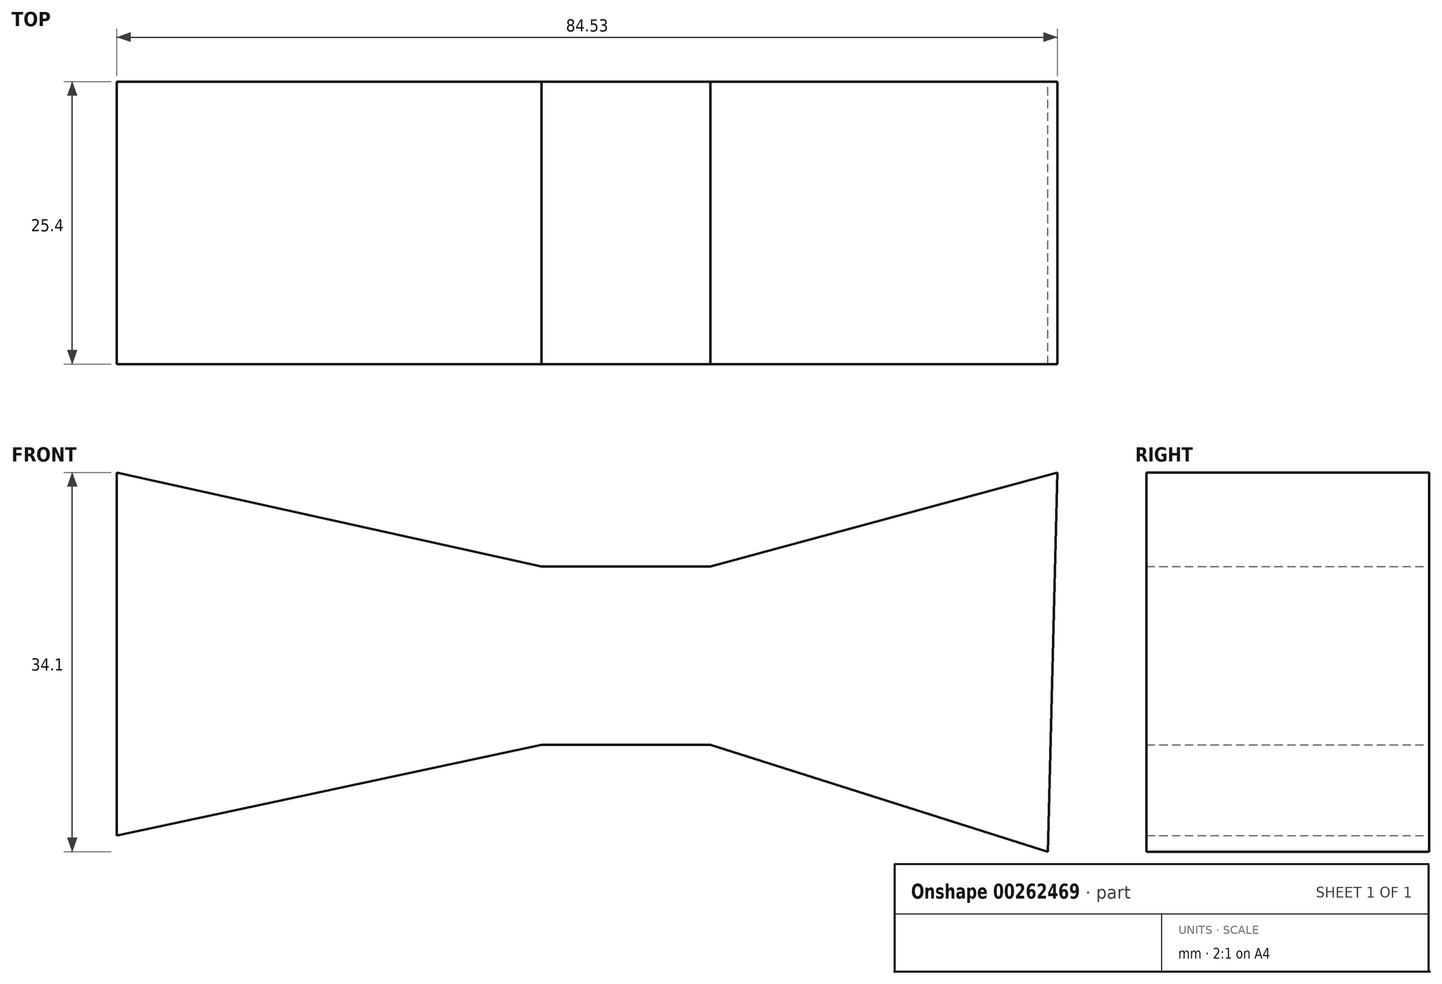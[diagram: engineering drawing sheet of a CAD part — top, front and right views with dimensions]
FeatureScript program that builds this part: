
annotation { "Feature Type Name" : "Feature", "Feature Type Description" : "" }
export const myFeature = defineFeature(function(context is Context, id is Id, definition is map)
    precondition{}
    {
        {
            var Q0;
            Q0=qCreatedBy(makeId("Front.planeOp"),FACE);
            var sketch = newSketch(context, id + "F0", { "sketchPlane" : qUnion([Q0])});
            skLineSegment(sketch, "E0.bottom", {"start": v(7.58, -8.02) * mm, "end": v(-7.58, -8.02) * mm});
            skLineSegment(sketch, "E0.top", {"start": v(7.58, 8.02) * mm, "end": v(-7.58, 8.02) * mm});
            skLineSegment(sketch, "E0.left", {"start": v(7.58, -8.02) * mm, "end": v(7.58, 8.02) * mm});
            skLineSegment(sketch, "E0.right", {"start": v(-7.58, -8.02) * mm, "end": v(-7.58, 8.02) * mm});
            skPoint(sketch, "E0.middle", {"position": v(0, 0) * mm});
            skLineSegment(sketch, "E1", {"start": v(-7.58, 8.02) * mm, "end": v(-45.76, 16.47) * mm});
            skLineSegment(sketch, "E2", {"start": v(-45.76, 16.47) * mm, "end": v(-45.76, -16.18) * mm});
            skLineSegment(sketch, "E3", {"start": v(-45.76, -16.18) * mm, "end": v(-7.58, -8.02) * mm});
            skLineSegment(sketch, "E4", {"start": v(7.58, 8.02) * mm, "end": v(38.77, 16.47) * mm});
            skLineSegment(sketch, "E5", {"start": v(7.58, -8.02) * mm, "end": v(37.9, -17.63) * mm});
            skLineSegment(sketch, "E6", {"start": v(37.9, -17.63) * mm, "end": v(38.77, 16.47) * mm});
            skSolve(sketch);
        }
        {
            var Q0;
            Q0 = qSketchRegion(id + "F0", true);
            extrude(context, id + "F1", {"entities" : qUnion([Q0]), "depth" : 25.4 * mm});
        }
        {
            var Q0;
            Q0 = qSketchRegion(id + "F0", true);
            extrude(context, id + "F2", {"entities" : qUnion([Q0]), "operationType" : NewBodyOperationType.ADD, "depth" : 25.4 * mm});
        }
        {
            var Q0;
            Q0 = qSketchRegion(id + "F0", true);
            extrude(context, id + "F3", {"entities" : qUnion([Q0]), "operationType" : NewBodyOperationType.ADD, "depth" : 25.4 * mm});
        }
    });
